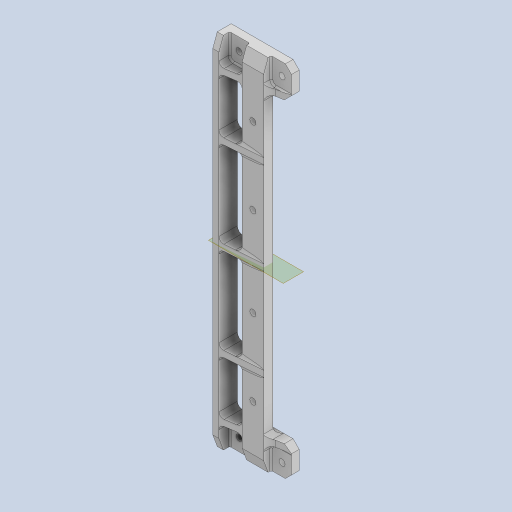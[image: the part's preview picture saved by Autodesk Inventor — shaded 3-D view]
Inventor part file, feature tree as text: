
AUTODESK INVENTOR PART (.ipt)
format: ipt  version: 2023 (Build 270158000, 158)  size: 589,312 bytes
history: native  units: mm
features: projected_geometry x8, sketch x7, extrude x6, fillet x6, chamfer x6, other x6, thicken_offset x5, reference x2, plane x1, pattern_linear x1, mirror x1, hole x1
ambient origin geometry x8: Origin, YZ Plane, XZ Plane, XY Plane, X Axis, Y Axis, Z Axis, Center Point
bodies: Solid1 (feature_tree)
feature tree (50):
  extrude  "Extrusion1"  Depth=2.0mm
  extrude  "Extrusion2"  Depth=2.0mm
  extrude  "Extrusion3"  Depth=7.0mm
  thicken_offset  "Thicken1"
  thicken_offset  "Thicken2"
  thicken_offset  "Thicken3"
  thicken_offset  "Thicken4"
  thicken_offset  "Thicken5"
  extrude  "Extrusion4"  Depth=4.0mm TaperAngle=0.0deg
  plane  "Work Plane1"
  extrude  "Extrusion5"  Depth=1.0mm
  pattern_linear  "Rectangular Pattern1"  Spacing1=0.5mm  [1 undecoded]
  extrude  "Extrusion6"  Depth=10.0mm
  mirror  "Mirror1"
  fillet  "Fillet1"  Radius=0.5mm
  fillet  "Fillet2"  Radius=0.5mm
  fillet  "Fillet3"  Radius=0.5mm
  chamfer  "Chamfer1"  Distance=0.5mm
  chamfer  "Chamfer2"  Distance=0.5mm
  chamfer  "Chamfer3"  Distance=6.0mm
  chamfer  "Chamfer4"  Distance=117.0mm
  chamfer  "Chamfer5"  Distance=2.0mm
  chamfer  "Chamfer6"  Distance=2.0mm
  fillet  "Fillet4"  Radius=20.0mm
  fillet  "Fillet5"  Radius=20.0mm
  fillet  "Fillet6"  Radius=2.0mm
  hole  "Hole1"  [1 undecoded]
  sketch  "Sketch1"  dims[d0=2.0mm d1=2.0mm]
  reference  "Reference1"
  reference  "Reference2"
  sketch  "Sketch2"  dims[d2=2.0mm d3=2.0mm]
  sketch  "Sketch3"  dims[d4=2.0mm d5=0.0mm d6=7.0mm]
  projected_geometry  "Projected Loop1"
  sketch  "Sketch4"  dims[d7=117.0mm d8=4.0mm d9=0.0mm]
  projected_geometry  "Projected Loop2"
  projected_geometry  "Projected Loop3"
  sketch  "Sketch5"  dims[d10=2.0mm d11=0.0mm d12=1.0mm]
  sketch  "Sketch6"  dims[d13=1.0mm]
  projected_geometry  "Projected Loop4"
  sketch  "Sketch7"  dims[d14=0.5mm d15=0.5mm d16=0.5mm d17=0.5mm d18=0.5mm d19=0.5mm d20=0.5mm d21=0.5mm d22=6.0mm d23=117.0mm d24=2.0mm d25=0.0mm d26=2.0mm d27=0.0mm d28=20.0mm d30=30.0mm d31=20.0mm d33=30.0mm d34=2.0mm d35=0.0mm d36=1.5mm d37=1.5mm d38=3.0mm d39=4.0mm d40=2.0mm d41=3.490659mm d42=4.0mm d43=2.0mm d44=3.490659mm d45=4.0mm d46=2.0mm d47=3.490659mm d48=4.0mm d49=2.0mm d50=3.490659mm d51=2.0mm d52=2.0mm d53=3.490659mm d54=2.0mm d55=2.0mm d56=3.490659mm d57=0.5mm d58=2.0mm d59=2.0mm d60=7.0mm d61=7.0mm d62=25.0mm d63=25.0mm d64=2.0mm d65=6.0mm d66=4.0mm d67=2.0mm d68=90.0deg d69=10.0mm d70=0.0mm]
  projected_geometry  "Projected Loop5"
  projected_geometry  "Projected Loop6"
  projected_geometry  "Projected Loop7"
  projected_geometry  "Projected Loop8"
  parser-record x1  (decoder bookkeeping rows leaked as tree rows — omitted from the tree; the rows remain in map.json)
  other  "body_8d_wid_1.iam"
  other  "leg_1_2d_MIR:1"
  other  "leg_holder_2_MIR:1"
  other  "leg_2d_1:1"
  other  "leg_holder_2:1"
note: 2 required parameter values undecoded (feature->parameter linkage not recoverable at this tier; creation-order binding heuristic only, values carry confidence <= 0.55)
note: 1 file-system path scrubbed to <path> (originals preserved in map.json)
